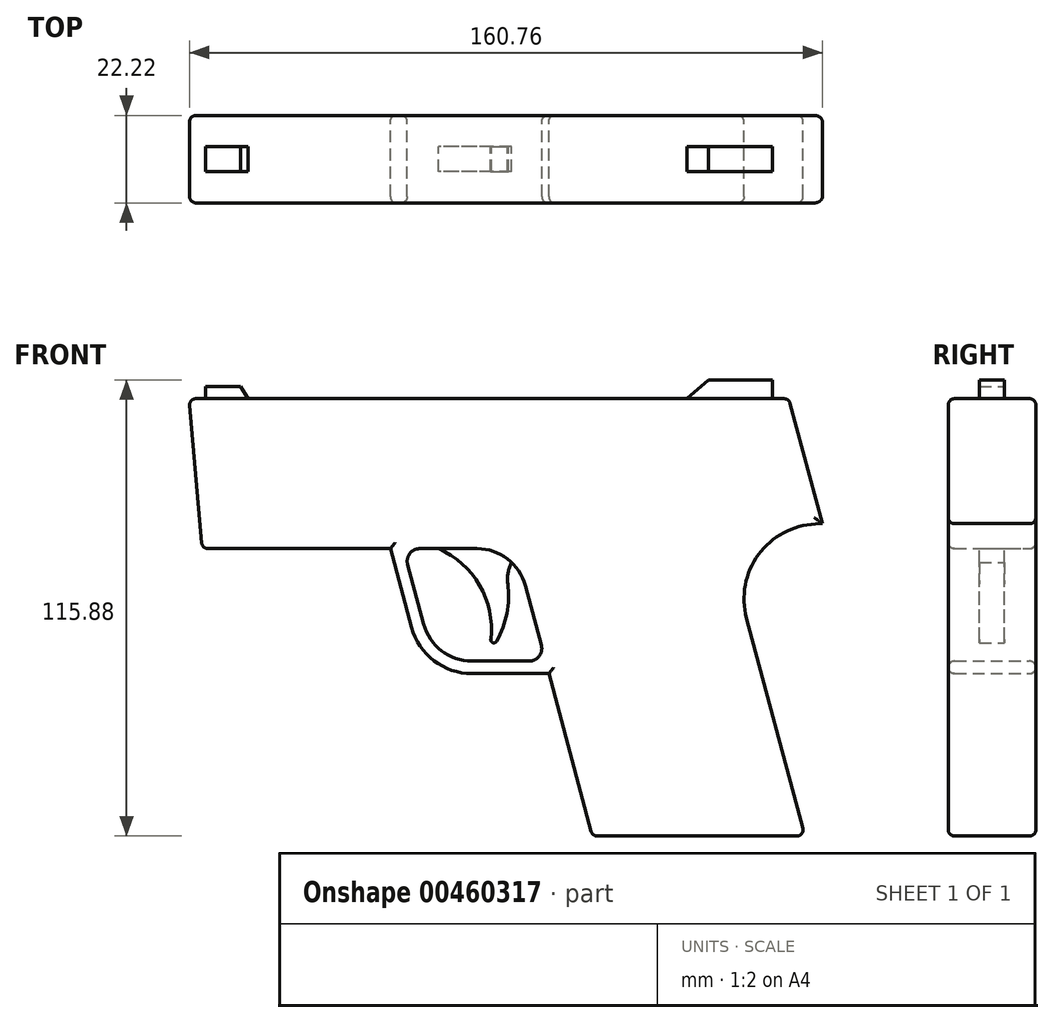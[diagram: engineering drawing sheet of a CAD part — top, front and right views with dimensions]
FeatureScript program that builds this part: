
annotation { "Feature Type Name" : "Feature", "Feature Type Description" : "" }
export const myFeature = defineFeature(function(context is Context, id is Id, definition is map)
    precondition{}
    {
        {
            var Q0;
            Q0=qCreatedBy(makeId("Front.planeOp"),FACE);
            var sketch = newSketch(context, id + "F0", { "sketchPlane" : qUnion([Q0])});
            skLineSegment(sketch, "E0", {"start": v(-45.68, 32.05) * mm, "end": v(106.72, 32.05) * mm});
            skLineSegment(sketch, "E1", {"start": v(106.72, 32.05) * mm, "end": v(115.22, 0.3) * mm});
            skLineSegment(sketch, "E2", {"start": v(115.22, 0.3) * mm, "end": v(113.48, 0.22) * mm});
            skLineSegment(sketch, "E3", {"start": v(95.95, -23.74) * mm, "end": v(110.78, -79.08) * mm});
            skLineSegment(sketch, "E4", {"start": v(110.78, -79.08) * mm, "end": v(56.8, -79.08) * mm});
            skLineSegment(sketch, "E5", {"start": v(56.8, -79.08) * mm, "end": v(45.75, -37.8) * mm});
            skLineSegment(sketch, "E6", {"start": v(45.75, -37.8) * mm, "end": v(26.18, -37.8) * mm});
            skLineSegment(sketch, "E7", {"start": v(10.84, -26.04) * mm, "end": v(5.49, -6.05) * mm});
            skLineSegment(sketch, "E8", {"start": v(5.49, -6.05) * mm, "end": v(-42.35, -6.05) * mm});
            skLineSegment(sketch, "E9", {"start": v(-42.35, -6.05) * mm, "end": v(-45.68, 32.05) * mm});
            skLineSegment(sketch, "E10", {"start": v(43.82, -30.63) * mm, "end": v(39.76, -15.47) * mm});
            skLineSegment(sketch, "E11", {"start": v(27.5, -6.05) * mm, "end": v(12.91, -6.05) * mm});
            skLineSegment(sketch, "E12", {"start": v(9.85, -10.05) * mm, "end": v(13.9, -25.22) * mm});
            skLineSegment(sketch, "E13", {"start": v(26.18, -34.63) * mm, "end": v(40.76, -34.63) * mm});
            skPoint(sketch, "E14.visualSharp", {"position": v(16.43, -34.63) * mm});
            skArc(sketch, "E14.filletArc", {"start": v(13.9, -25.22) * mm, "mid": v(18.45, -32) * mm, "end": v(26.18, -34.63) * mm});
            skPoint(sketch, "E15.visualSharp", {"position": v(14, -37.8) * mm});
            skArc(sketch, "E15.filletArc", {"start": v(10.84, -26.04) * mm, "mid": v(16.51, -34.52) * mm, "end": v(26.18, -37.8) * mm});
            skPoint(sketch, "E16.visualSharp", {"position": v(37.24, -6.05) * mm});
            skArc(sketch, "E16.filletArc", {"start": v(39.76, -15.47) * mm, "mid": v(35.22, -8.68) * mm, "end": v(27.5, -6.05) * mm});
            skPoint(sketch, "E17.visualSharp", {"position": v(8.78, -6.05) * mm});
            skArc(sketch, "E17.filletArc", {"start": v(12.91, -6.05) * mm, "mid": v(10.4, -7.3) * mm, "end": v(9.85, -10.05) * mm});
            skPoint(sketch, "E18.visualSharp", {"position": v(44.9, -34.63) * mm});
            skArc(sketch, "E18.filletArc", {"start": v(40.76, -34.63) * mm, "mid": v(43.28, -33.39) * mm, "end": v(43.82, -30.63) * mm});
            skPoint(sketch, "E19.visualSharp", {"position": v(89.82, -0.87) * mm});
            skArc(sketch, "E19.filletArc", {"start": v(113.48, 0.22) * mm, "mid": v(98.98, -7.57) * mm, "end": v(95.95, -23.74) * mm});
            skSolve(sketch);
        }
        {
            var Q0;
            Q0 = qSketchRegion(id + "F0", true);
            extrude(context, id + "F1", {"entities" : qUnion([Q0]), "endBound" : BoundingType.SYMMETRIC, "depth" : 22.22 * mm});
        }
        {
            var Q0;
            Q0=makeQuery(id+"F1.opExtrude","SWEPT_EDGE",EDGE,{"disambiguationData":[OSD([sQuery(id+"F0.wireOp",EDGE,"E0"),sQuery(id+"F0.wireOp",EDGE,"E9")])]});
            var Q1;
            Q1=makeQuery(id+"F1.opExtrude","SWEPT_EDGE",EDGE,{"disambiguationData":[OSD([sQuery(id+"F0.wireOp",EDGE,"E8"),sQuery(id+"F0.wireOp",EDGE,"E9")])]});
            var Q2;
            Q2=makeQuery(id+"F1.opExtrude","SWEPT_EDGE",EDGE,{"disambiguationData":[OSD([sQuery(id+"F0.wireOp",EDGE,"E4"),sQuery(id+"F0.wireOp",EDGE,"E5")])]});
            var Q3;
            Q3=makeQuery(id+"F1.opExtrude","SWEPT_EDGE",EDGE,{"disambiguationData":[OSD([sQuery(id+"F0.wireOp",EDGE,"E3"),sQuery(id+"F0.wireOp",EDGE,"E4")])]});
            var Q4;
            Q4=makeQuery(id+"F1.opExtrude","CAP_EDGE",EDGE,{"disambiguationData":[OSD([sQuery(id+"F0.wireOp",EDGE,"E0")])],"isStart":false});
            var Q5;
            Q5=makeQuery(id+"F1.opExtrude","CAP_EDGE",EDGE,{"disambiguationData":[OSD([sQuery(id+"F0.wireOp",EDGE,"E9")])],"isStart":false});
            var Q6;
            Q6=makeQuery(id+"F1.opExtrude","CAP_EDGE",EDGE,{"disambiguationData":[OSD([sQuery(id+"F0.wireOp",EDGE,"E8")])],"isStart":false});
            var Q7;
            Q7=makeQuery(id+"F1.opExtrude","CAP_EDGE",EDGE,{"disambiguationData":[OSD([sQuery(id+"F0.wireOp",EDGE,"E7")])],"isStart":false});
            var Q8;
            Q8=makeQuery(id+"F1.opExtrude","CAP_EDGE",EDGE,{"disambiguationData":[OSD([sQuery(id+"F0.wireOp",EDGE,"E6")])],"isStart":false});
            var Q9;
            Q9=makeQuery(id+"F1.opExtrude","CAP_EDGE",EDGE,{"disambiguationData":[OSD([sQuery(id+"F0.wireOp",EDGE,"E5")])],"isStart":false});
            var Q10;
            Q10=makeQuery(id+"F1.opExtrude","CAP_EDGE",EDGE,{"disambiguationData":[OSD([sQuery(id+"F0.wireOp",EDGE,"E4")])],"isStart":false});
            var Q11;
            Q11=makeQuery(id+"F1.opExtrude","CAP_EDGE",EDGE,{"disambiguationData":[OSD([sQuery(id+"F0.wireOp",EDGE,"E3")])],"isStart":false});
            var Q12;
            Q12=makeQuery(id+"F1.opExtrude","CAP_EDGE",EDGE,{"disambiguationData":[OSD([sQuery(id+"F0.wireOp",EDGE,"E2")])],"isStart":false});
            var Q13;
            Q13=makeQuery(id+"F1.opExtrude","CAP_EDGE",EDGE,{"disambiguationData":[OSD([sQuery(id+"F0.wireOp",EDGE,"E1")])],"isStart":false});
            var Q14;
            Q14=makeQuery(id+"F1.opExtrude","CAP_EDGE",EDGE,{"disambiguationData":[OSD([sQuery(id+"F0.wireOp",EDGE,"E13")])],"isStart":false});
            var Q15;
            Q15=makeQuery(id+"F1.opExtrude","CAP_EDGE",EDGE,{"disambiguationData":[OSD([sQuery(id+"F0.wireOp",EDGE,"E10")])],"isStart":false});
            var Q16;
            Q16=makeQuery(id+"F1.opExtrude","CAP_EDGE",EDGE,{"disambiguationData":[OSD([sQuery(id+"F0.wireOp",EDGE,"E11")])],"isStart":false});
            var Q17;
            Q17=makeQuery(id+"F1.opExtrude","CAP_EDGE",EDGE,{"disambiguationData":[OSD([sQuery(id+"F0.wireOp",EDGE,"E1")])],"isStart":true});
            var Q18;
            Q18=makeQuery(id+"F1.opExtrude","CAP_EDGE",EDGE,{"disambiguationData":[OSD([sQuery(id+"F0.wireOp",EDGE,"E2")])],"isStart":true});
            var Q19;
            Q19=makeQuery(id+"F1.opExtrude","CAP_EDGE",EDGE,{"disambiguationData":[OSD([sQuery(id+"F0.wireOp",EDGE,"E3")])],"isStart":true});
            var Q20;
            Q20=makeQuery(id+"F1.opExtrude","CAP_EDGE",EDGE,{"disambiguationData":[OSD([sQuery(id+"F0.wireOp",EDGE,"E4")])],"isStart":true});
            var Q21;
            Q21=makeQuery(id+"F1.opExtrude","CAP_EDGE",EDGE,{"disambiguationData":[OSD([sQuery(id+"F0.wireOp",EDGE,"E5")])],"isStart":true});
            var Q22;
            Q22=makeQuery(id+"F1.opExtrude","CAP_EDGE",EDGE,{"disambiguationData":[OSD([sQuery(id+"F0.wireOp",EDGE,"E6")])],"isStart":true});
            var Q23;
            Q23=makeQuery(id+"F1.opExtrude","CAP_EDGE",EDGE,{"disambiguationData":[OSD([sQuery(id+"F0.wireOp",EDGE,"E7")])],"isStart":true});
            var Q24;
            Q24=makeQuery(id+"F1.opExtrude","CAP_EDGE",EDGE,{"disambiguationData":[OSD([sQuery(id+"F0.wireOp",EDGE,"E8")])],"isStart":true});
            var Q25;
            Q25=makeQuery(id+"F1.opExtrude","CAP_EDGE",EDGE,{"disambiguationData":[OSD([sQuery(id+"F0.wireOp",EDGE,"E11")])],"isStart":true});
            var Q26;
            Q26=makeQuery(id+"F1.opExtrude","CAP_EDGE",EDGE,{"disambiguationData":[OSD([sQuery(id+"F0.wireOp",EDGE,"E12")])],"isStart":true});
            var Q27;
            Q27=makeQuery(id+"F1.opExtrude","CAP_EDGE",EDGE,{"disambiguationData":[OSD([sQuery(id+"F0.wireOp",EDGE,"E13")])],"isStart":true});
            var Q28;
            Q28=makeQuery(id+"F1.opExtrude","CAP_EDGE",EDGE,{"disambiguationData":[OSD([sQuery(id+"F0.wireOp",EDGE,"E10")])],"isStart":true});
            var Q29;
            Q29=makeQuery(id+"F1.opExtrude","CAP_EDGE",EDGE,{"disambiguationData":[OSD([sQuery(id+"F0.wireOp",EDGE,"E0")])],"isStart":true});
            var Q30;
            Q30=makeQuery(id+"F1.opExtrude","CAP_EDGE",EDGE,{"disambiguationData":[OSD([sQuery(id+"F0.wireOp",EDGE,"E9")])],"isStart":true});
            var Q31;
            Q31=makeQuery(id+"F1.opExtrude","SWEPT_EDGE",EDGE,{"disambiguationData":[OSD([sQuery(id+"F0.wireOp",EDGE,"E0"),sQuery(id+"F0.wireOp",EDGE,"E1")])]});
            fillet(context, id + "F2", {"entities" : qUnion([Q0, Q1, Q2, Q3, Q4, Q5, Q6, Q7, Q8, Q9, Q10, Q11, Q12, Q13, Q14, Q15, Q16, Q17, Q18, Q19, Q20, Q21, Q22, Q23, Q24, Q25, Q26, Q27, Q28, Q29, Q30, Q31]), "radius" : 1.59 * mm, "tangentPropagation" : true, "allowEdgeOverflow" : false});
        }
        {
            var Q0;
            Q0=qCreatedBy(makeId("Front.planeOp"),FACE);
            var sketch = newSketch(context, id + "F3", { "sketchPlane" : qUnion([Q0])});
            skArc(sketch, "E20", {"start": v(30.97, -29.1) * mm, "mid": v(25.51, -11.72) * mm, "end": v(8.9, -4.26) * mm});
            skArc(sketch, "E21", {"start": v(32.45, -29.58) * mm, "mid": v(35.04, -22.5) * mm, "end": v(35.3, -14.97) * mm});
            skArc(sketch, "E22", {"start": v(44.75, -4.26) * mm, "mid": v(37.6, -7.48) * mm, "end": v(35.3, -14.97) * mm});
            skLineSegment(sketch, "E23.trimOffspring", {"start": v(8.9, -4.26) * mm, "end": v(44.75, -4.26) * mm});
            skArc(sketch, "E24", {"start": v(30.97, -29.1) * mm, "mid": v(31.51, -29.94) * mm, "end": v(32.45, -29.58) * mm});
            skLineSegment(sketch, "E25", {"start": v(-41.5, 30.13) * mm, "end": v(-41.5, 35.19) * mm});
            skLineSegment(sketch, "E26", {"start": v(-41.5, 35.19) * mm, "end": v(-32.55, 35.19) * mm});
            skLineSegment(sketch, "E27", {"start": v(-32.55, 35.19) * mm, "end": v(-29.1, 29.44) * mm});
            skLineSegment(sketch, "E28", {"start": v(-29.1, 29.44) * mm, "end": v(-41.5, 30.13) * mm});
            skLineSegment(sketch, "E29", {"start": v(78.4, 29.9) * mm, "end": v(86.22, 36.8) * mm});
            skLineSegment(sketch, "E30", {"start": v(86.22, 36.8) * mm, "end": v(102.53, 36.8) * mm});
            skLineSegment(sketch, "E31", {"start": v(102.53, 36.8) * mm, "end": v(102.53, 27.6) * mm});
            skLineSegment(sketch, "E32", {"start": v(102.53, 27.6) * mm, "end": v(78.4, 29.9) * mm});
            skSolve(sketch);
        }
        {
            var Q0;
            Q0 = qSketchRegion(id + "F3", true);
            extrude(context, id + "F4", {"entities" : qUnion([Q0]), "operationType" : NewBodyOperationType.ADD, "endBound" : BoundingType.SYMMETRIC, "depth" : 6.35 * mm});
        }
    });
